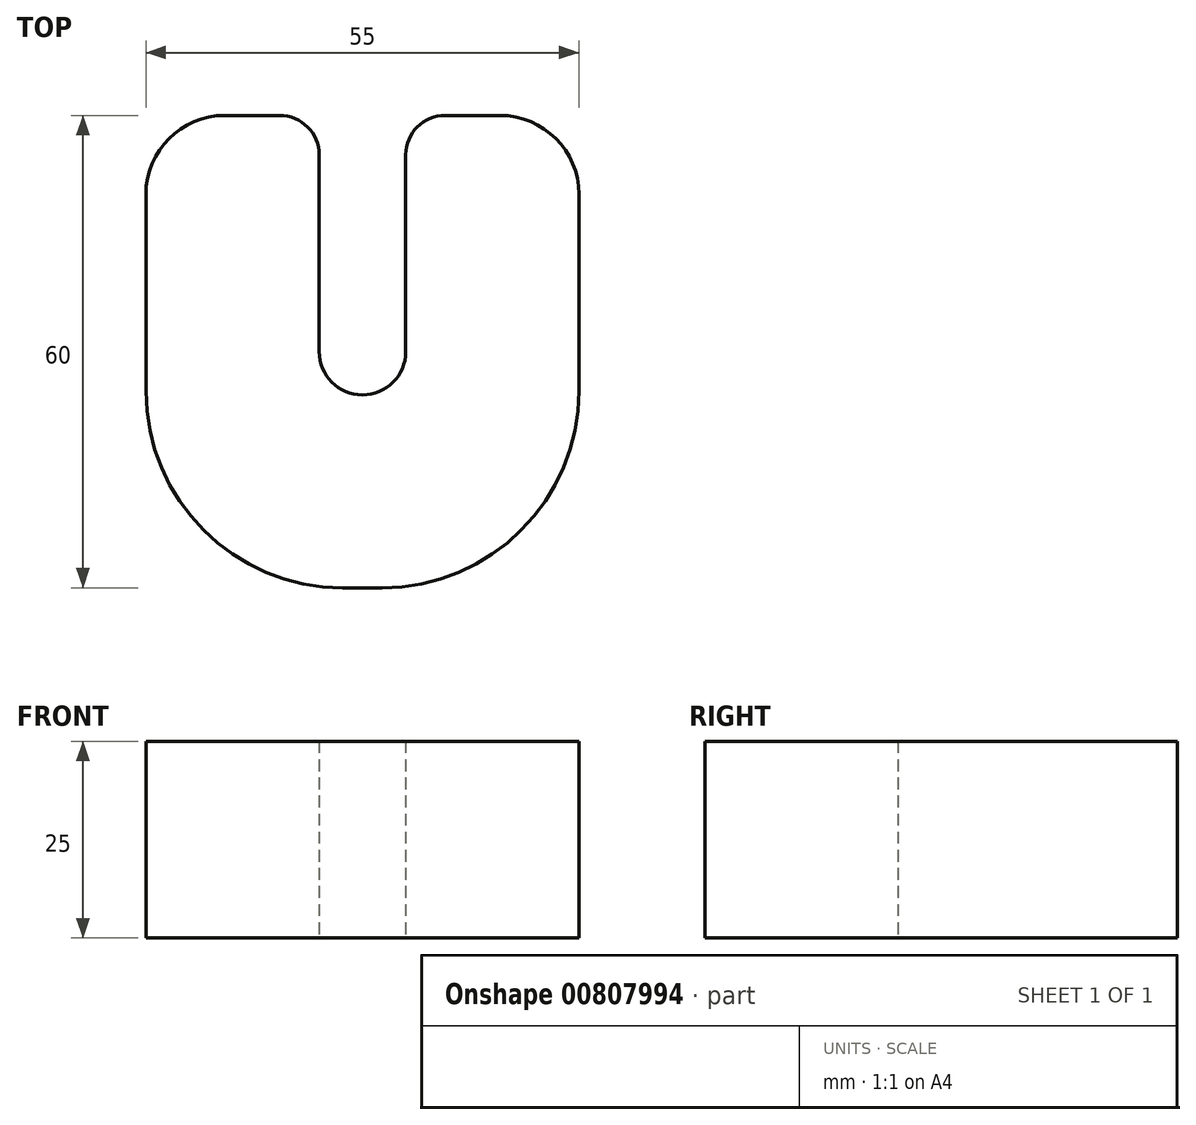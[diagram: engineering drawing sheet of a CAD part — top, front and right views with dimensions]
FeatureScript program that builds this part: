
annotation { "Feature Type Name" : "Feature", "Feature Type Description" : "" }
export const myFeature = defineFeature(function(context is Context, id is Id, definition is map)
    precondition{}
    {
        {
            var Q0;
            Q0=qCreatedBy(makeId("Top.planeOp"),FACE);
            var sketch = newSketch(context, id + "F0", { "sketchPlane" : qUnion([Q0])});
            skLineSegment(sketch, "E0.bottom", {"start": v(25, 0) * mm, "end": v(30, 0) * mm});
            skLineSegment(sketch, "E0.top", {"start": v(10, 60) * mm, "end": v(17, 60) * mm});
            skLineSegment(sketch, "E0.left", {"start": v(0, 25) * mm, "end": v(0, 50) * mm});
            skLineSegment(sketch, "E0.right", {"start": v(55, 25) * mm, "end": v(55, 50) * mm});
            skLineSegment(sketch, "E1", {"start": v(27.5, 60) * mm, "end": v(27.5, 0) * mm, "construction": true});
            skArc(sketch, "E2", {"start": v(22, 30) * mm, "mid": v(27.5, 24.5) * mm, "end": v(33, 30) * mm});
            skLineSegment(sketch, "E3", {"start": v(22, 30) * mm, "end": v(22, 55) * mm});
            skLineSegment(sketch, "E4", {"start": v(33, 30) * mm, "end": v(33, 55) * mm});
            skLineSegment(sketch, "E5.trimOffspring", {"start": v(38, 60) * mm, "end": v(45, 60) * mm});
            skPoint(sketch, "E6.visualSharp", {"position": v(22, 60) * mm});
            skArc(sketch, "E6.filletArc", {"start": v(22, 55) * mm, "mid": v(20.54, 58.54) * mm, "end": v(17, 60) * mm});
            skPoint(sketch, "E7.visualSharp", {"position": v(33, 60) * mm});
            skArc(sketch, "E7.filletArc", {"start": v(38, 60) * mm, "mid": v(34.46, 58.54) * mm, "end": v(33, 55) * mm});
            skPoint(sketch, "E8.visualSharp", {"position": v(0, 0) * mm});
            skArc(sketch, "E8.filletArc", {"start": v(0, 25) * mm, "mid": v(7.32, 7.32) * mm, "end": v(25, 0) * mm});
            skPoint(sketch, "E9.visualSharp", {"position": v(55, 0) * mm});
            skArc(sketch, "E9.filletArc", {"start": v(30, 0) * mm, "mid": v(47.68, 7.32) * mm, "end": v(55, 25) * mm});
            skPoint(sketch, "E10.visualSharp", {"position": v(0, 60) * mm});
            skArc(sketch, "E10.filletArc", {"start": v(10, 60) * mm, "mid": v(2.93, 57.07) * mm, "end": v(0, 50) * mm});
            skPoint(sketch, "E11.visualSharp", {"position": v(55, 60) * mm});
            skArc(sketch, "E11.filletArc", {"start": v(55, 50) * mm, "mid": v(52.07, 57.07) * mm, "end": v(45, 60) * mm});
            skSolve(sketch);
        }
        {
            var Q0;
            Q0 = qSketchRegion(id + "F0", true);
            extrude(context, id + "F1", {"entities" : qUnion([Q0]), "depth" : 25 * mm, "offsetDistance" : 25 * mm});
        }
    });
